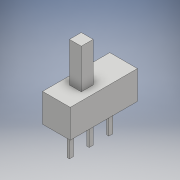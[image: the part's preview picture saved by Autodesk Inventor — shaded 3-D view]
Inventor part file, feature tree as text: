
AUTODESK INVENTOR PART (.ipt)
format: ipt  version: 2018 (Build 220112000, 112)  size: 127,488 bytes
history: native  units: mm
features: extrude x3, sketch x3, other x1
ambient origin geometry x8: Origin, YZ Plane, XZ Plane, XY Plane, X Axis, Y Axis, Z Axis, Center Point
bodies: Body1 (feature_tree)
feature tree (7):
  other  "ソリッド1"
  extrude  "押し出し1"  Depth=8.5mm
  extrude  "押し出し2"  Depth=3.5mm
  extrude  "押し出し3"  Depth=3.6mm TaperAngle=0.0deg
  sketch  "スケッチ1"
  sketch  "スケッチ2"
  sketch  "スケッチ3"
